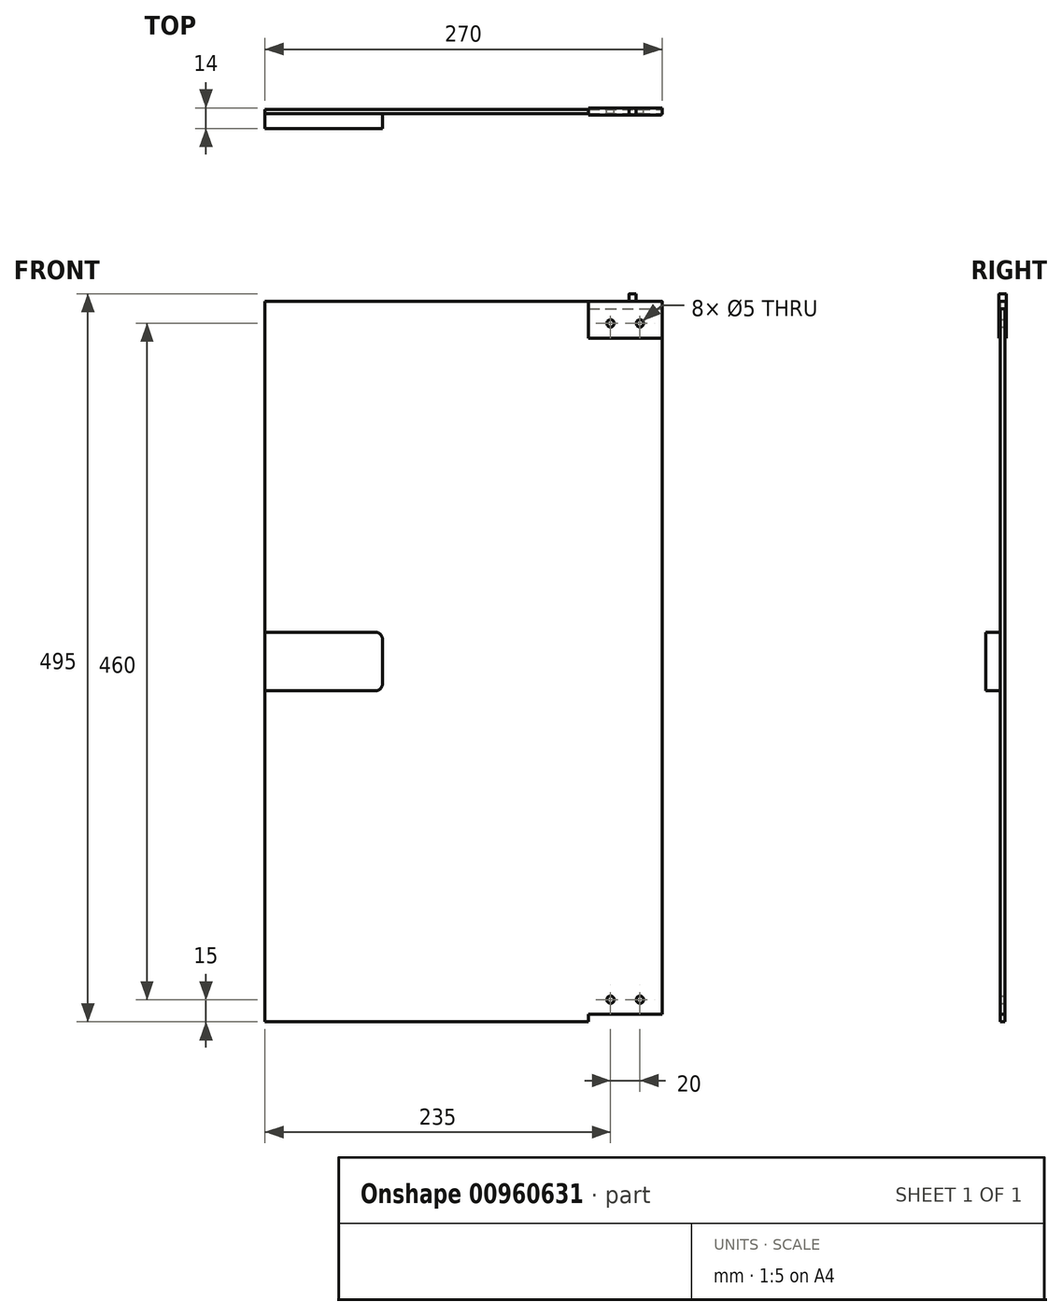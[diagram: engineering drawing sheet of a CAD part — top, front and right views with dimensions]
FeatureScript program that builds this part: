
annotation { "Feature Type Name" : "Feature", "Feature Type Description" : "" }
export const myFeature = defineFeature(function(context is Context, id is Id, definition is map)
    precondition{}
    {
        {
            var Q0;
            Q0=qCreatedBy(makeId("Right.planeOp"),FACE);
            var sketch = newSketch(context, id + "F0", { "sketchPlane" : qUnion([Q0])});
            skPoint(sketch, "E0.middle", {"position": v(0, 0) * mm});
            skLineSegment(sketch, "E1", {"start": v(2.5, -12.5) * mm, "end": v(1.5, -12.5) * mm});
            skLineSegment(sketch, "E2", {"start": v(1.5, -12.5) * mm, "end": v(1.5, 7.5) * mm});
            skLineSegment(sketch, "E3", {"start": v(1.5, 7.5) * mm, "end": v(-1.5, 7.5) * mm});
            skLineSegment(sketch, "E4", {"start": v(-1.5, 7.5) * mm, "end": v(-1.5, -12.5) * mm});
            skLineSegment(sketch, "E5", {"start": v(-1.5, -12.5) * mm, "end": v(-2.5, -12.5) * mm});
            skLineSegment(sketch, "E6", {"start": v(-2.5, 12.5) * mm, "end": v(2.5, 12.5) * mm});
            skLineSegment(sketch, "E7", {"start": v(-2.5, 12.5) * mm, "end": v(-2.5, -12.5) * mm});
            skLineSegment(sketch, "E8", {"start": v(2.5, 12.5) * mm, "end": v(2.5, -12.5) * mm});
            skSolve(sketch);
        }
        {
            var Q0;
            Q0=makeQuery(id+"F0.imprint","IMPRINT",FACE,{"disambiguationData":[TD([[makeQuery(id+"F0.imprint","IMPRINT",EDGE,{"derivedFrom":sQuery(id+"F0.wireOp",EDGE,"E1")}),-1.0]])]});
            extrude(context, id + "F1", {"entities" : qUnion([Q0]), "oppositeDirection" : true, "depth" : 50 * mm, "offsetDistance" : 25 * mm});
        }
        {
            var Q0;
            Q0=makeQuery(id+"F1.opExtrude","SWEPT_FACE",FACE,{"disambiguationData":[OSD([sQuery(id+"F0.wireOp",EDGE,"E6")])]});
            var sketch = newSketch(context, id + "F2", { "sketchPlane" : qUnion([Q0])});
            skCircle(sketch, "E9", {"center": v(-20, 0) * mm, "radius": 2.5 * mm});
            skPoint(sketch, "E9.centerSnap0", {"position": v(0, 0) * mm});
            skSolve(sketch);
        }
        {
            var Q0;
            {var subQ0=sQuery(id+"F2.wireOp",EDGE,"E9");var subQ1=sQuery(id+"F0.wireOp",EDGE,"E6");var subQ2=makeQuery(id+"F2.imprint","INTERSECT",VERTEX,{"derivedFrom":[makeQuery(id+"F1.opExtrude","SWEPT_EDGE",EDGE,{"disambiguationData":[OSD([subQ1,sQuery(id+"F0.wireOp",EDGE,"E7")])]}),subQ0]});Q0=makeQuery(id+"F2.imprint","IMPRINT",FACE,{"disambiguationData":[TD([[makeQuery(id+"F2.imprint","IMPRINT",EDGE,{"disambiguationData":[TD([[subQ2,1.0]])],"derivedFrom":subQ0}),1.0]])]});}
            var Q1;
            Q1=sQuery(id+"F2.wireOp",EDGE,"E9");
            extrude(context, id + "F3", {"entities" : qUnion([Q0]), "operationType" : NewBodyOperationType.ADD, "surfaceEntities" : qUnion([Q1]), "depth" : 5 * mm, "offsetDistance" : 25 * mm});
        }
        {
            var Q0;
            Q0=makeQuery(id+"F1.opExtrude","SWEPT_FACE",FACE,{"disambiguationData":[OSD([sQuery(id+"F0.wireOp",EDGE,"E7")])]});
            var sketch = newSketch(context, id + "F4", { "sketchPlane" : qUnion([Q0])});
            skCircle(sketch, "E10", {"center": v(-35, -2.5) * mm, "radius": 2.5 * mm});
            skCircle(sketch, "E11", {"center": v(-15, -2.5) * mm, "radius": 2.5 * mm});
            skSolve(sketch);
        }
        {
            var Q0;
            Q0=makeQuery(id+"F4.imprint","IMPRINT",FACE,{"disambiguationData":[TD([[makeQuery(id+"F4.imprint","IMPRINT",EDGE,{"derivedFrom":sQuery(id+"F4.wireOp",EDGE,"E10")}),1.0]])]});
            var Q1;
            Q1=makeQuery(id+"F4.imprint","IMPRINT",FACE,{"disambiguationData":[TD([[makeQuery(id+"F4.imprint","IMPRINT",EDGE,{"derivedFrom":sQuery(id+"F4.wireOp",EDGE,"E11")}),1.0]])]});
            extrude(context, id + "F5", {"entities" : qUnion([Q0, Q1]), "operationType" : NewBodyOperationType.REMOVE, "oppositeDirection" : true, "depth" : 25 * mm, "offsetDistance" : 25 * mm});
        }
        {
            var Q0;
            Q0=qCreatedBy(makeId("Front.planeOp"),FACE);
            var sketch = newSketch(context, id + "F6", { "sketchPlane" : qUnion([Q0])});
            skLineSegment(sketch, "E12", {"start": v(-50, 12.5) * mm, "end": v(-50, 7.5) * mm});
            skLineSegment(sketch, "E13", {"start": v(-50, 7.5) * mm, "end": v(0, 7.5) * mm});
            skLineSegment(sketch, "E14", {"start": v(-270, 12.5) * mm, "end": v(-50, 12.5) * mm});
            skCircle(sketch, "E15", {"center": v(-15, -2.5) * mm, "radius": 2.5 * mm});
            skCircle(sketch, "E16", {"center": v(-35, -2.5) * mm, "radius": 2.5 * mm});
            skLineSegment(sketch, "E17", {"start": v(-330.71, -232.5) * mm, "end": v(92.47, -232.5) * mm, "construction": true});
            skLineSegment(sketch, "E18", {"start": v(0, 7.5) * mm, "end": v(0, -232.5) * mm});
            skLineSegment(sketch, "E19", {"start": v(-270, 12.5) * mm, "end": v(-270, -232.5) * mm});
            skCircle(sketch, "E20.MirrorC", {"center": v(-15, -462.5) * mm, "radius": 2.5 * mm});
            skCircle(sketch, "E21.MirrorC", {"center": v(-35, -462.5) * mm, "radius": 2.5 * mm});
            skLineSegment(sketch, "E22.MirrorCS", {"start": v(-50, -477.5) * mm, "end": v(-50, -472.5) * mm});
            skLineSegment(sketch, "E23.MirrorCS", {"start": v(0, -472.5) * mm, "end": v(0, -232.5) * mm});
            skLineSegment(sketch, "E24.MirrorCS", {"start": v(-50, -472.5) * mm, "end": v(0, -472.5) * mm});
            skLineSegment(sketch, "E25.MirrorCS", {"start": v(-270, -477.5) * mm, "end": v(-270, -232.5) * mm});
            skLineSegment(sketch, "E26.MirrorCS", {"start": v(-270, -477.5) * mm, "end": v(-50, -477.5) * mm});
            skCircle(sketch, "E27", {"center": v(-250, -232.5) * mm, "radius": 5 * mm});
            skCircle(sketch, "E28", {"center": v(-220, -232.5) * mm, "radius": 5 * mm});
            skSolve(sketch);
        }
        {
            var Q0;
            Q0=makeQuery(id+"F6.imprint","IMPRINT",FACE,{"disambiguationData":[TD([[makeQuery(id+"F6.imprint","IMPRINT",EDGE,{"derivedFrom":sQuery(id+"F6.wireOp",EDGE,"E12")}),-1.0]])]});
            extrude(context, id + "F7", {"entities" : qUnion([Q0]), "endBound" : BoundingType.SYMMETRIC, "depth" : 3 * mm, "offsetDistance" : 25 * mm});
        }
        {
            var Q0;
            Q0=makeQuery(id+"F7.opExtrude","CAP_FACE",FACE,{"disambiguationData":[OSD([sQuery(id+"F6.wireOp",EDGE,"E12"),sQuery(id+"F6.wireOp",EDGE,"E13"),sQuery(id+"F6.wireOp",EDGE,"E14"),sQuery(id+"F6.wireOp",EDGE,"E15"),sQuery(id+"F6.wireOp",EDGE,"E16"),sQuery(id+"F6.wireOp",EDGE,"E18"),sQuery(id+"F6.wireOp",EDGE,"E19"),sQuery(id+"F6.wireOp",EDGE,"E20.MirrorC"),sQuery(id+"F6.wireOp",EDGE,"E21.MirrorC"),sQuery(id+"F6.wireOp",EDGE,"E22.MirrorCS"),sQuery(id+"F6.wireOp",EDGE,"E23.MirrorCS"),sQuery(id+"F6.wireOp",EDGE,"E24.MirrorCS"),sQuery(id+"F6.wireOp",EDGE,"E25.MirrorCS"),sQuery(id+"F6.wireOp",EDGE,"E26.MirrorCS"),sQuery(id+"F6.wireOp",EDGE,"E27"),sQuery(id+"F6.wireOp",EDGE,"E28")])],"isStart":false});
            var sketch = newSketch(context, id + "F8", { "sketchPlane" : qUnion([Q0])});
            skLineSegment(sketch, "E29.bottom", {"start": v(-190, -252.5) * mm, "end": v(-270, -252.5) * mm});
            skLineSegment(sketch, "E29.top", {"start": v(-190, -212.5) * mm, "end": v(-270, -212.5) * mm});
            skLineSegment(sketch, "E29.left", {"start": v(-190, -252.5) * mm, "end": v(-190, -212.5) * mm});
            skLineSegment(sketch, "E29.right", {"start": v(-270, -252.5) * mm, "end": v(-270, -212.5) * mm});
            skCircle(sketch, "E30", {"center": v(-250, -232.5) * mm, "radius": 5 * mm});
            skCircle(sketch, "E31", {"center": v(-220, -232.5) * mm, "radius": 5 * mm});
            skSolve(sketch);
        }
        {
            var Q0;
            Q0=makeQuery(id+"F8.imprint","IMPRINT",FACE,{"disambiguationData":[TD([[makeQuery(id+"F8.imprint","IMPRINT",EDGE,{"derivedFrom":sQuery(id+"F8.wireOp",EDGE,"E29.bottom")}),-1.0]])]});
            var Q1;
            Q1=makeQuery(id+"F8.imprint","IMPRINT",FACE,{"disambiguationData":[TD([[makeQuery(id+"F8.imprint","IMPRINT",EDGE,{"derivedFrom":sQuery(id+"F8.wireOp",EDGE,"E30")}),1.0]])]});
            var Q2;
            Q2=makeQuery(id+"F8.imprint","IMPRINT",FACE,{"disambiguationData":[TD([[makeQuery(id+"F8.imprint","IMPRINT",EDGE,{"derivedFrom":sQuery(id+"F8.wireOp",EDGE,"E31")}),1.0]])]});
            extrude(context, id + "F9", {"entities" : qUnion([Q0, Q1, Q2]), "depth" : 10 * mm, "offsetDistance" : 25 * mm});
        }
        {
            var Q0;
            Q0=makeQuery(id+"F8.imprint","IMPRINT",FACE,{"disambiguationData":[TD([[makeQuery(id+"F8.imprint","IMPRINT",EDGE,{"derivedFrom":sQuery(id+"F8.wireOp",EDGE,"E30")}),1.0]])]});
            var Q1;
            Q1=makeQuery(id+"F8.imprint","IMPRINT",FACE,{"disambiguationData":[TD([[makeQuery(id+"F8.imprint","IMPRINT",EDGE,{"derivedFrom":sQuery(id+"F8.wireOp",EDGE,"E31")}),1.0]])]});
            extrude(context, id + "F10", {"entities" : qUnion([Q0, Q1]), "operationType" : NewBodyOperationType.ADD, "oppositeDirection" : true, "depth" : 3 * mm, "offsetDistance" : 25 * mm});
        }
        {
            var Q0;
            Q0=makeQuery(id+"F9.opExtrude","SWEPT_EDGE",EDGE,{"disambiguationData":[OSD([sQuery(id+"F8.wireOp",EDGE,"E29.top"),sQuery(id+"F8.wireOp",EDGE,"E29.left")])]});
            var Q1;
            Q1=makeQuery(id+"F9.opExtrude","SWEPT_EDGE",EDGE,{"disambiguationData":[OSD([sQuery(id+"F8.wireOp",EDGE,"E29.bottom"),sQuery(id+"F8.wireOp",EDGE,"E29.left")])]});
            fillet(context, id + "F11", {"entities" : qUnion([Q0, Q1]), "tangentPropagation" : true, "radius" : 5 * mm, "defaultsChanged" : false, "vertexSettings" : [], "allowEdgeOverflow" : false});
        }
        {
            var Q0;
            Q0=makeQuery(id+"F1.opExtrude","CAP_EDGE",EDGE,{"disambiguationData":[OSD([sQuery(id+"F0.wireOp",EDGE,"E7")])],"isStart":true});
            fillet(context, id + "F12", {"entities" : qUnion([Q0]), "tangentPropagation" : true, "radius" : 1 * mm, "defaultsChanged" : true, "vertexSettings" : [], "allowEdgeOverflow" : false});
        }
    });
